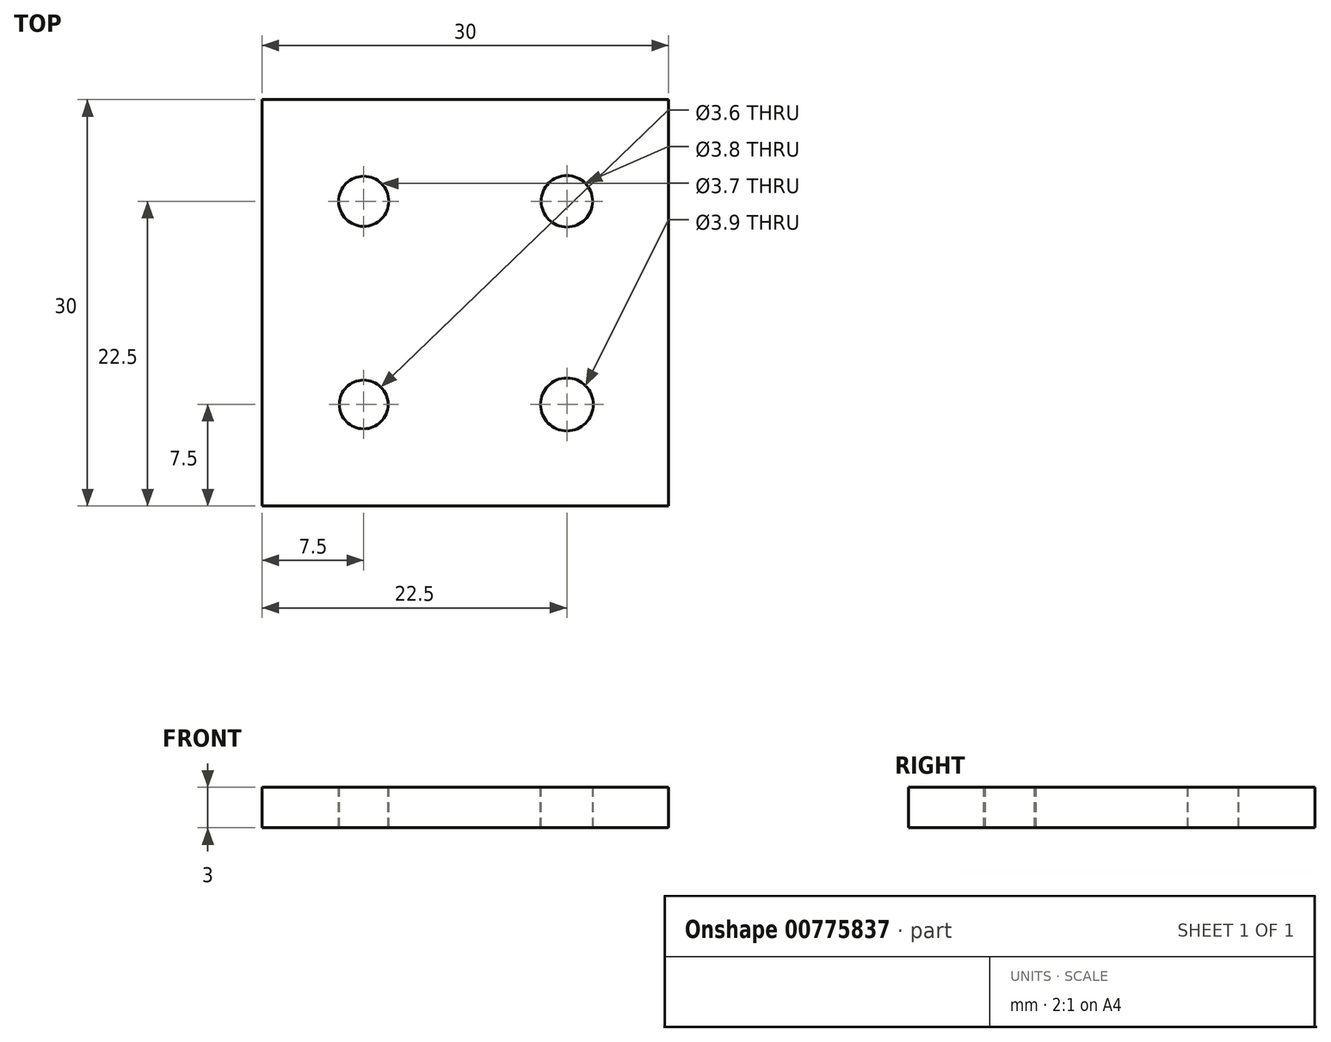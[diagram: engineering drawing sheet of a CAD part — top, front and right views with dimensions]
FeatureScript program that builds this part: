
annotation { "Feature Type Name" : "Feature", "Feature Type Description" : "" }
export const myFeature = defineFeature(function(context is Context, id is Id, definition is map)
    precondition{}
    {
        {
            var Q0;
            Q0=qCreatedBy(makeId("Top.planeOp"),FACE);
            var sketch = newSketch(context, id + "F0", { "sketchPlane" : qUnion([Q0])});
            skLineSegment(sketch, "E0.bottom", {"start": v(-15, 15) * mm, "end": v(15, 15) * mm});
            skLineSegment(sketch, "E0.top", {"start": v(-15, -15) * mm, "end": v(15, -15) * mm});
            skLineSegment(sketch, "E0.left", {"start": v(-15, 15) * mm, "end": v(-15, -15) * mm});
            skLineSegment(sketch, "E0.right", {"start": v(15, 15) * mm, "end": v(15, -15) * mm});
            skPoint(sketch, "E0.middle", {"position": v(0, 0) * mm});
            skSolve(sketch);
        }
        {
            assignVariable(context, id + "F1", {"name" : "thick", "anyValue" : 3 * mm});
        }
        {
            var Q0;
            Q0=qSketchRegion(id+"F0",true);
            extrude(context, id + "F2", {"entities" : qUnion([Q0]), "depth" : getVariable(context, 'thick'), "offsetDistance" : 25 * mm});
        }
        {
            var Q0;
            Q0=makeQuery(id+"F2.opExtrude","CAP_FACE",FACE,{"disambiguationData":[OSD([sQuery(id+"F0.wireOp",EDGE,"E0.bottom"),sQuery(id+"F0.wireOp",EDGE,"E0.top"),sQuery(id+"F0.wireOp",EDGE,"E0.left"),sQuery(id+"F0.wireOp",EDGE,"E0.right")])],"isStart":false});
            var sketch = newSketch(context, id + "F3", { "sketchPlane" : qUnion([Q0])});
            skLineSegment(sketch, "E1.bottom", {"start": v(-15, -15) * mm, "end": v(-7.5, -15) * mm, "construction": true});
            skLineSegment(sketch, "E1.top", {"start": v(-15, -7.5) * mm, "end": v(-7.5, -7.5) * mm, "construction": true});
            skLineSegment(sketch, "E1.left", {"start": v(-15, -15) * mm, "end": v(-15, -7.5) * mm, "construction": true});
            skLineSegment(sketch, "E1.right", {"start": v(-7.5, -15) * mm, "end": v(-7.5, -7.5) * mm, "construction": true});
            skCircle(sketch, "E2", {"center": v(-7.5, -7.5) * mm, "radius": 1.8 * mm});
            skLineSegment(sketch, "E3.bottom", {"start": v(15, -15) * mm, "end": v(7.5, -15) * mm, "construction": true});
            skLineSegment(sketch, "E3.top", {"start": v(15, -7.5) * mm, "end": v(7.5, -7.5) * mm, "construction": true});
            skLineSegment(sketch, "E3.left", {"start": v(15, -15) * mm, "end": v(15, -7.5) * mm, "construction": true});
            skLineSegment(sketch, "E3.right", {"start": v(7.5, -15) * mm, "end": v(7.5, -7.5) * mm, "construction": true});
            skCircle(sketch, "E4", {"center": v(7.5, -7.5) * mm, "radius": 1.95 * mm});
            skLineSegment(sketch, "E5.bottom", {"start": v(-15, 15) * mm, "end": v(-7.5, 15) * mm, "construction": true});
            skLineSegment(sketch, "E5.top", {"start": v(-15, 7.5) * mm, "end": v(-7.5, 7.5) * mm, "construction": true});
            skLineSegment(sketch, "E5.left", {"start": v(-15, 15) * mm, "end": v(-15, 7.5) * mm, "construction": true});
            skLineSegment(sketch, "E5.right", {"start": v(-7.5, 15) * mm, "end": v(-7.5, 7.5) * mm, "construction": true});
            skLineSegment(sketch, "E6.bottom", {"start": v(15, 15) * mm, "end": v(7.5, 15) * mm, "construction": true});
            skLineSegment(sketch, "E6.top", {"start": v(15, 7.5) * mm, "end": v(7.5, 7.5) * mm, "construction": true});
            skLineSegment(sketch, "E6.left", {"start": v(15, 15) * mm, "end": v(15, 7.5) * mm, "construction": true});
            skLineSegment(sketch, "E6.right", {"start": v(7.5, 15) * mm, "end": v(7.5, 7.5) * mm, "construction": true});
            skCircle(sketch, "E7", {"center": v(-7.5, 7.5) * mm, "radius": 1.85 * mm});
            skCircle(sketch, "E8", {"center": v(7.5, 7.5) * mm, "radius": 1.9 * mm});
            skSolve(sketch);
        }
        {
            var Q0;
            Q0=makeQuery(id+"F3.imprint","IMPRINT",FACE,{"disambiguationData":[TD([[makeQuery(id+"F3.imprint","IMPRINT",EDGE,{"derivedFrom":sQuery(id+"F3.wireOp",EDGE,"E2")}),1.0]])]});
            var Q1;
            Q1=makeQuery(id+"F3.imprint","IMPRINT",FACE,{"disambiguationData":[TD([[makeQuery(id+"F3.imprint","IMPRINT",EDGE,{"derivedFrom":sQuery(id+"F3.wireOp",EDGE,"E4")}),1.0]])]});
            var Q2;
            Q2=makeQuery(id+"F3.imprint","IMPRINT",FACE,{"disambiguationData":[TD([[makeQuery(id+"F3.imprint","IMPRINT",EDGE,{"derivedFrom":sQuery(id+"F3.wireOp",EDGE,"E7")}),1.0]])]});
            var Q3;
            Q3=makeQuery(id+"F3.imprint","IMPRINT",FACE,{"disambiguationData":[TD([[makeQuery(id+"F3.imprint","IMPRINT",EDGE,{"derivedFrom":sQuery(id+"F3.wireOp",EDGE,"E8")}),1.0]])]});
            extrude(context, id + "F4", {"entities" : qUnion([Q0, Q1, Q2, Q3]), "operationType" : NewBodyOperationType.REMOVE, "oppositeDirection" : true, "depth" : getVariable(context, 'thick'), "offsetDistance" : 25 * mm});
        }
    });
